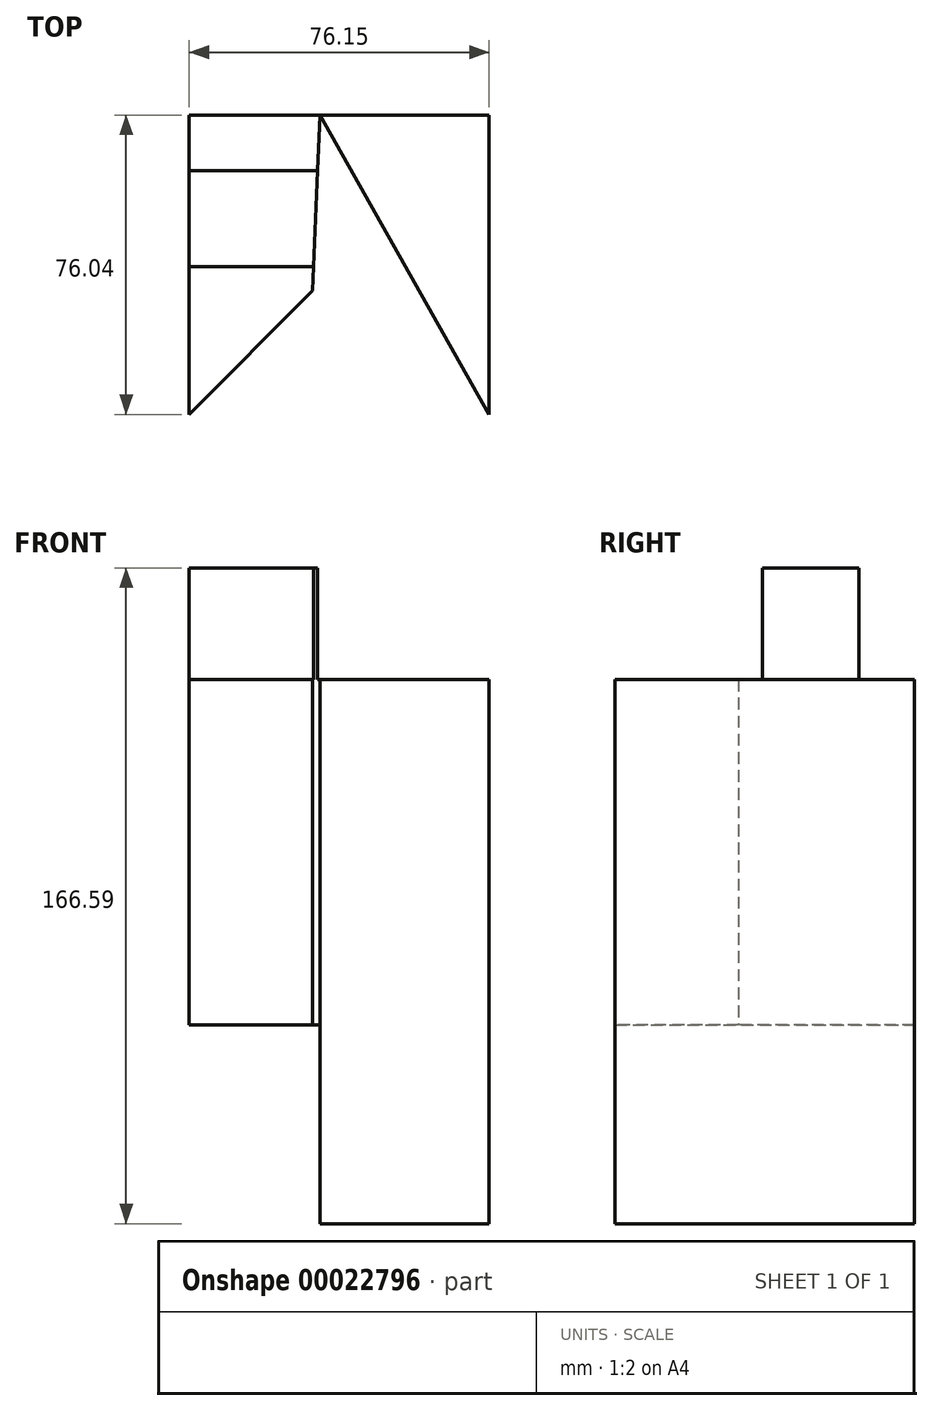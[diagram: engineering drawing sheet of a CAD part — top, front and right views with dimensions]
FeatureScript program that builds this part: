
annotation { "Feature Type Name" : "Feature", "Feature Type Description" : "" }
export const myFeature = defineFeature(function(context is Context, id is Id, definition is map)
    precondition{}
    {
        {
            var Q0;
            Q0=qCreatedBy(makeId("Top.planeOp"),FACE);
            var sketch = newSketch(context, id + "F0", { "sketchPlane" : qUnion([Q0])});
            skLineSegment(sketch, "E0", {"start": v(0, 76.04) * mm, "end": v(75.71, 76.04) * mm});
            skLineSegment(sketch, "E1", {"start": v(75.71, 76.04) * mm, "end": v(0, 0) * mm});
            skLineSegment(sketch, "E2", {"start": v(0, 0) * mm, "end": v(0, 76.04) * mm});
            skLineSegment(sketch, "E3", {"start": v(33.17, 76.04) * mm, "end": v(31.29, 31.42) * mm});
            skSolve(sketch);
        }
        {
            var Q0;
            {var subQ1=sQuery(id+"F0.wireOp",EDGE,"E2");Q0=makeQuery(id+"F0.imprint","IMPRINT",FACE,{"disambiguationData":[TD([[makeQuery(id+"F0.imprint","IMPRINT",EDGE,{"derivedFrom":subQ1}),-1.0]])]});}
            extrude(context, id + "F1", {"entities" : qUnion([Q0]), "depth" : 87.74 * mm});
        }
        {
            var Q0;
            Q0=makeQuery(id+"F1.opExtrude","CAP_FACE",FACE,{"disambiguationData":[OSD([sQuery(id+"F0.wireOp",EDGE,"E0"),sQuery(id+"F0.wireOp",EDGE,"E1"),sQuery(id+"F0.wireOp",EDGE,"E2"),sQuery(id+"F0.wireOp",EDGE,"E3")])],"isStart":false});
            var sketch = newSketch(context, id + "F2", { "sketchPlane" : qUnion([Q0])});
            skLineSegment(sketch, "E4", {"start": v(33.17, 76.04) * mm, "end": v(76.15, 76.04) * mm});
            skLineSegment(sketch, "E5", {"start": v(76.15, 76.04) * mm, "end": v(76.15, 0) * mm});
            skLineSegment(sketch, "E6", {"start": v(76.15, 0) * mm, "end": v(33.17, 76.04) * mm});
            skSolve(sketch);
        }
        {
            var Q0;
            Q0=makeQuery(id+"F2.imprint","IMPRINT",FACE,{"disambiguationData":[TD([[makeQuery(id+"F2.imprint","IMPRINT",EDGE,{"derivedFrom":sQuery(id+"F2.wireOp",EDGE,"E4")}),-1.0]])]});
            extrude(context, id + "F3", {"entities" : qUnion([Q0]), "oppositeDirection" : true, "depth" : 138.24 * mm});
        }
        {
            var Q0;
            Q0=makeQuery(id+"F1.opExtrude","CAP_FACE",FACE,{"disambiguationData":[OSD([sQuery(id+"F0.wireOp",EDGE,"E0"),sQuery(id+"F0.wireOp",EDGE,"E1"),sQuery(id+"F0.wireOp",EDGE,"E2"),sQuery(id+"F0.wireOp",EDGE,"E3")])],"isStart":false});
            var sketch = newSketch(context, id + "F4", { "sketchPlane" : qUnion([Q0])});
            skLineSegment(sketch, "E7", {"start": v(0, 61.94) * mm, "end": v(32.58, 61.94) * mm});
            skLineSegment(sketch, "E8", {"start": v(32.58, 61.94) * mm, "end": v(31.54, 37.51) * mm});
            skLineSegment(sketch, "E9", {"start": v(31.54, 37.51) * mm, "end": v(0, 37.51) * mm});
            skLineSegment(sketch, "E10", {"start": v(0, 37.51) * mm, "end": v(0, 61.94) * mm});
            skSolve(sketch);
        }
        {
            var Q0;
            Q0=makeQuery(id+"F4.imprint","IMPRINT",FACE,{"disambiguationData":[TD([[makeQuery(id+"F4.imprint","IMPRINT",EDGE,{"derivedFrom":sQuery(id+"F4.wireOp",EDGE,"E7")}),-1.0]])]});
            extrude(context, id + "F5", {"entities" : qUnion([Q0]), "operationType" : NewBodyOperationType.ADD, "depth" : 28.36 * mm});
        }
    });
